# Revit family: NBS_Allermuir_OffcChrs_AxylChair-en-us
name_source: partatom
category: Furniture
revit_build: Autodesk Revit 2016 (Build: 20151007_0715(x64)
units: mm (PartAtom-declared; Revit-internal decimal feet)

## family parameters
Always vertical = Yes
Cut with Voids When Loaded = No
Room Calculation Point = No
Shared = No
Work Plane-Based = No

## types (1)
- AXL02
    AssetType = Moveable
    BIMObjectName = NBS_Allermuir_OfficeChairs_Axyl_AXL02-US
    Category = Pr_40_50_12_57:Office chairs
    Description = Arm chair
    DurationUnit = year
    ExpectedLife = 5
    Features = Stacks 4, Stacking buffers, Plastic Glides
    FootHeight = 0 "
    FrameColour = Black, white, sage, basalt, peacock blue, coral, pebble, stone, polished aluminium, raw aluminium
    FrameFinishOptions = Powder coat, polished aluminium, raw aluminium
    FrameMaterials = Aluminium
    FrameMountingMaterial = NBS_Concept
    HighestSeatingHeight = 0 "
    IfcExportAs = IfcFurnitureType
    IfcExportType = CHAIR
    IsBuiltIn = No
    LegHeight = 15 "
    LowestSeatingHeight = 0 "
    ManufacturerName = Allermuir
    ManufacturerURL = www.allermuir.com
    Material = Aluminium
    ModelNumber = AXL02
    ModelReference = Axyl
    NBSCertification = www.nationalbimlibrary.com/cert/iu2unp5z
    NBSDescription = Office chairs
    NBSReference = 45-35-20/330
    Name = OfficeChairs_Axyl_AXL02-US_Allermuir
    NominalDepth = 24 "
    NominalHeight = 31 "
    NominalLength = 22 "
    NominalWidth = 24 "
    OmniClassCode = 22-12 62 19
    OmniClassTitle = Stacking Chairs
    OmniClassVersion = Table 22 2012-05-16
    OptionalFeatures = Glides with felt
    SeatFrameMaterial = NBS_Concept
    SeatingHeight = 18 "
    SeatingSeatMaterial = NBS_Concept
    SeatsAndBacksColour = Black, white, sage, basalt, peacock blue, coral (plastic); pebble, stone (wood fibre)
    SeatsAndBacksMaterial = Plastic
    SeatsAndBacksMaterialOptions = Plastic, Wood fibre injected plastic
    Size = 22.25 x 23.75 x 30.75"
    StandardsDurability = ANSI/BIFMA X5.1 - 2011
    StandardsSafetyRequirements = ANSI/BIFMA X5.1 - 2011
    Status = UNSET
    Uniclass2015Code = Pr_40_50_12_57
    Uniclass2015Title = Office chairs
    Uniclass2015Version = Products v1.9
    Version = 1
    WarrantyDescription = Allermuir warrant that its manufactured products are free from manufacturing defects - in materials or workmanship - for a period of five (5) years. , Allermuir will repair, or replace (at Allermuir's sole discretion) with comparable free of charge materials / components, any product / component which fails under normal use in a single shift environment, as a result of a defect in the materials and/ or workmanship
    WarrantyDurationParts = 5
    WarrantyDurationUnit = year

## geometry (parser evidence)
native form markers: Sweep x10
no freeform markers — native parametric forms only
